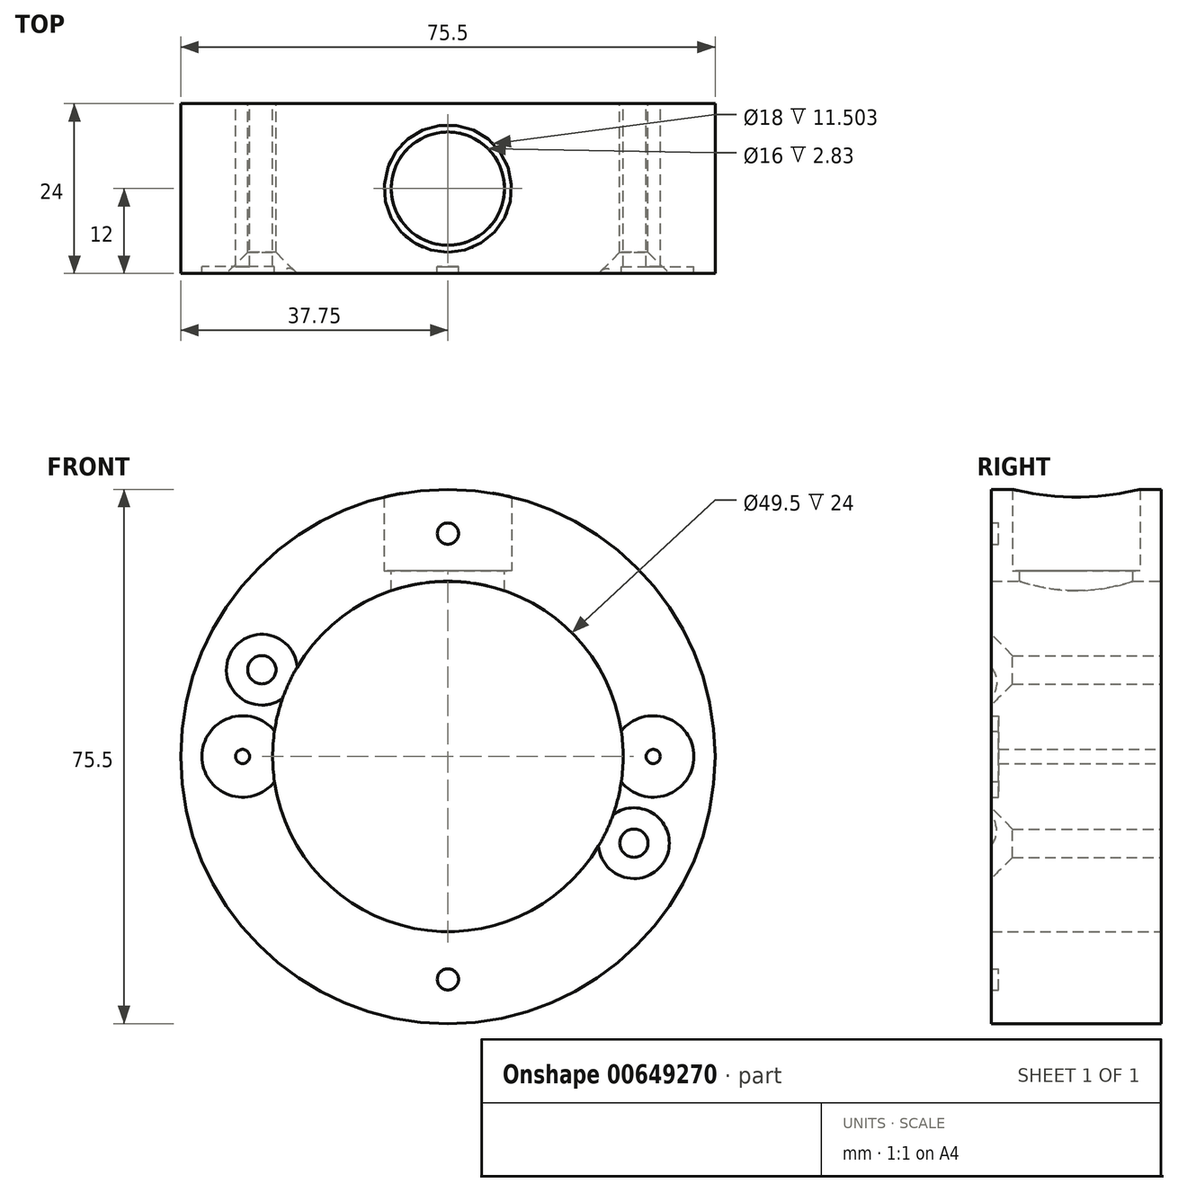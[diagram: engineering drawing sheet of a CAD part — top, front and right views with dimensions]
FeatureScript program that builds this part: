
annotation { "Feature Type Name" : "Feature", "Feature Type Description" : "" }
export const myFeature = defineFeature(function(context is Context, id is Id, definition is map)
    precondition{}
    {
        {
            var Q0;
            Q0=qCreatedBy(makeId("Front.planeOp"),FACE);
            var sketch = newSketch(context, id + "F0", { "sketchPlane" : qUnion([Q0])});
            skCircle(sketch, "E0", {"center": v(0, 0) * mm, "radius": 37.75 * mm});
            skCircle(sketch, "E1.0", {"center": v(0, 0) * mm, "radius": 24.75 * mm});
            skCircle(sketch, "E2", {"center": v(-29, 0) * mm, "radius": 1 * mm});
            skCircle(sketch, "E3", {"center": v(29, 0) * mm, "radius": 1 * mm});
            skCircle(sketch, "E4", {"center": v(-29, 0) * mm, "radius": 5.75 * mm});
            skCircle(sketch, "E5", {"center": v(29, 0) * mm, "radius": 5.75 * mm});
            skCircle(sketch, "E6", {"center": v(-26.28, 12.26) * mm, "radius": 2 * mm});
            skCircle(sketch, "E7", {"center": v(26.28, -12.26) * mm, "radius": 2 * mm});
            skLineSegment(sketch, "E8", {"start": v(0, 0) * mm, "end": v(-26.28, 12.26) * mm});
            skLineSegment(sketch, "E9", {"start": v(0, 0) * mm, "end": v(10.46, 22.43) * mm});
            skCircle(sketch, "E10", {"center": v(0, -31.5) * mm, "radius": 1.5 * mm});
            skCircle(sketch, "E11", {"center": v(0, 31.5) * mm, "radius": 1.5 * mm});
            skSolve(sketch);
        }
        {
            var Q0;
            Q0 = qSketchRegion(id + "F0", true);
            extrude(context, id + "F1", {"entities" : qUnion([Q0]), "depth" : 24 * mm, "offsetDistance" : 25 * mm});
        }
        {
            var Q0;
            Q0=makeQuery(id+"F0.imprint","IMPRINT",FACE,{"disambiguationData":[TD([[makeQuery(id+"F0.imprint","IMPRINT",EDGE,{"derivedFrom":sQuery(id+"F0.wireOp",EDGE,"E2")}),-1.0]])]});
            var Q1;
            Q1=makeQuery(id+"F0.imprint","IMPRINT",FACE,{"disambiguationData":[TD([[makeQuery(id+"F0.imprint","IMPRINT",EDGE,{"derivedFrom":sQuery(id+"F0.wireOp",EDGE,"E11")}),1.0]])]});
            var Q2;
            Q2=makeQuery(id+"F0.imprint","IMPRINT",FACE,{"disambiguationData":[TD([[makeQuery(id+"F0.imprint","IMPRINT",EDGE,{"derivedFrom":sQuery(id+"F0.wireOp",EDGE,"E3")}),-1.0]])]});
            var Q3;
            Q3=makeQuery(id+"F0.imprint","IMPRINT",FACE,{"disambiguationData":[TD([[makeQuery(id+"F0.imprint","IMPRINT",EDGE,{"derivedFrom":sQuery(id+"F0.wireOp",EDGE,"E10")}),1.0]])]});
            extrude(context, id + "F2", {"entities" : qUnion([Q0, Q1, Q2, Q3]), "operationType" : NewBodyOperationType.ADD, "depth" : 23 * mm, "offsetDistance" : 25 * mm});
        }
        {
            var Q0;
            Q0=makeQuery(id+"F1.opExtrude","CAP_EDGE",EDGE,{"disambiguationData":[OSD([sQuery(id+"F0.wireOp",EDGE,"E6")])],"isStart":false});
            var Q1;
            Q1=makeQuery(id+"F1.opExtrude","CAP_EDGE",EDGE,{"disambiguationData":[OSD([sQuery(id+"F0.wireOp",EDGE,"E7")])],"isStart":false});
            chamfer(context, id + "F3", {"entities" : qUnion([Q0, Q1]), "width" : 3 * mm, "tangentPropagation" : true});
        }
        {
            var Q0;
            Q0=qCreatedBy(makeId("Top.planeOp"),FACE);
            cPlane(context, id + "F4", {"entities" : qUnion([Q0]), "cplaneType" : CPlaneType.OFFSET, "offset" : 26.25 * mm, "width" : 150 * mm, "height" : 150 * mm});
        }
        {
            var Q0;
            Q0=qCreatedBy(id+"F4.planeOp",FACE);
            var sketch = newSketch(context, id + "F5", { "sketchPlane" : qUnion([Q0])});
            skCircle(sketch, "E12", {"center": v(0, -12) * mm, "radius": 9 * mm});
            skCircle(sketch, "E13", {"center": v(0, -12) * mm, "radius": 8 * mm});
            skSolve(sketch);
        }
        {
            var Q0;
            Q0 = qSketchRegion(id + "F5", true);
            extrude(context, id + "F6", {"entities" : qUnion([Q0]), "operationType" : NewBodyOperationType.REMOVE, "oppositeDirection" : true, "depth" : -25 * mm, "offsetDistance" : 25 * mm});
        }
        {
            var Q0;
            Q0=makeQuery(id+"F5.imprint","IMPRINT",FACE,{"disambiguationData":[TD([[makeQuery(id+"F5.imprint","IMPRINT",EDGE,{"derivedFrom":sQuery(id+"F5.wireOp",EDGE,"E13")}),1.0]])]});
            extrude(context, id + "F7", {"entities" : qUnion([Q0]), "operationType" : NewBodyOperationType.REMOVE, "endBound" : BoundingType.SYMMETRIC, "oppositeDirection" : true, "depth" : 30 * mm, "offsetDistance" : 25 * mm});
        }
    });
